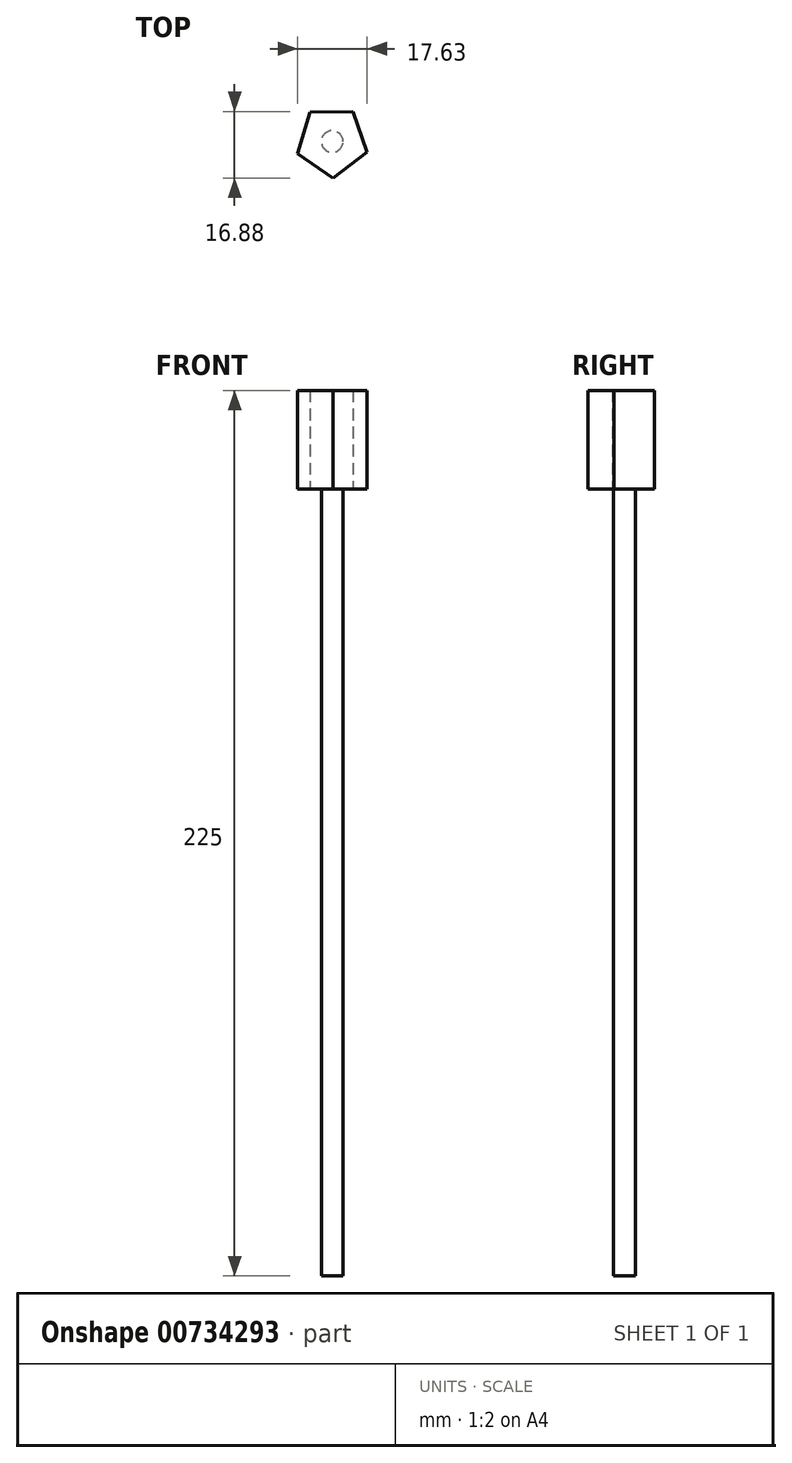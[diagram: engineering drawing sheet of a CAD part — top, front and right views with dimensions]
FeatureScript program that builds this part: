
annotation { "Feature Type Name" : "Feature", "Feature Type Description" : "" }
export const myFeature = defineFeature(function(context is Context, id is Id, definition is map)
    precondition{}
    {
        {
            var Q0;
            Q0=qCreatedBy(makeId("Top.planeOp"),FACE);
            var sketch = newSketch(context, id + "F0", { "sketchPlane" : qUnion([Q0])});
            skCircle(sketch, "E0", {"center": v(0, 0) * mm, "radius": 2.75 * mm});
            skSolve(sketch);
        }
        {
            var Q0;
            Q0 = qSketchRegion(id + "F0", true);
            extrude(context, id + "F1", {"entities" : qUnion([Q0]), "depth" : 200 * mm, "offsetDistance" : 25 * mm});
        }
        {
            var Q0;
            Q0=makeQuery(id+"F1.opExtrude","CAP_FACE",FACE,{"disambiguationData":[OSD([sQuery(id+"F0.wireOp",EDGE,"E0")])],"isStart":false});
            var sketch = newSketch(context, id + "F2", { "sketchPlane" : qUnion([Q0])});
            skCircle(sketch, "E1.cCircle", {"center": v(0, 0) * mm, "radius": 7.5 * mm, "construction": true});
            skLineSegment(sketch, "E1.0", {"start": v(8.88, -2.68) * mm, "end": v(0.2, -9.27) * mm});
            skLineSegment(sketch, "E1.1", {"start": v(0.2, -9.27) * mm, "end": v(-8.75, -3.05) * mm});
            skLineSegment(sketch, "E1.2", {"start": v(-8.75, -3.05) * mm, "end": v(-5.6, 7.38) * mm});
            skLineSegment(sketch, "E1.3", {"start": v(-5.6, 7.38) * mm, "end": v(5.3, 7.61) * mm});
            skLineSegment(sketch, "E1.4", {"start": v(5.3, 7.61) * mm, "end": v(8.88, -2.68) * mm});
            skPoint(sketch, "E1.0.midPoint", {"position": v(4.54, -5.97) * mm});
            skSolve(sketch);
        }
        {
            var Q0;
            Q0 = qSketchRegion(id + "F2", true);
            extrude(context, id + "F3", {"entities" : qUnion([Q0]), "operationType" : NewBodyOperationType.ADD, "depth" : 25 * mm, "offsetDistance" : 25 * mm});
        }
    });
